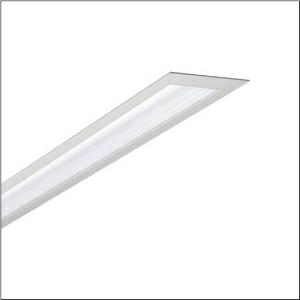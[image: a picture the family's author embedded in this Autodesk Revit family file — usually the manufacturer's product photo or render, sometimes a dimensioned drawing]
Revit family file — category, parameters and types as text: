
# Revit family: silica_r_5mx11dd1w4a_74f3
name_source: partatom
category: Lighting Fixtures
units: mm (PartAtom-declared; Revit-internal decimal feet)

## family parameters
Cut with Voids When Loaded = No
Host = Face
Light Source = No
Part Type = Normal
Room Calculation Point = No
Round Connector Dimension = Use Diameter
Shared = No

## types (1)
- --- (1 x LED, 3140 lm, 22.6 W, 4000K)
    Apparent Load = 23 VA
    CIE Flux Codes = 47 79 96 100 100
    Color Rendering = 80
    Color Temperature = 4000K
    Default Elevation = 1800 mm
    Description = Silica®, office luminaire, of aluminium, opal, light emission: direct distribution, primary light characteristic: symmetric, installation type: recessed, LED rated luminous flux: 3.010 lm, light colour: 840, colour temperature: 4000K, control gear: ECG DALI, with terminal, 3+2-pole, max. 2.5mm², mains connection: 230V, AC, 50/60Hz, rated input power: 24W, luminaire housing, of aluminium, matt pure white (RAL 9010), length: 1.462 mm, width: 93 mm, height: 60mm, end cap, of diecast zinc, pure white (RAL 9010), protection rating (complete): IP20, insulation class (complete): insulation class I (protective earthing), certification: CE, permissible ambient temperature for indoor applications: 0..+35°C, standard: EN 50419, packaging unit: 1 piece
    Height = 0 mm  [stored 0 ft]
    Lamp = 1 x LED
    Lamp Light Flux = 3140 lm
    Lamp Power = 22.6 W
    Lamp count = 1
    Length = 1462 mm
    Luminous efficacy = 139 lm/W
    Manufacturer = Siteco
    ModVariant = No
    Model = 5MX11DD1W4A
    Mounting Place = Ceiling
    Mounting Type = Recessed
    Number of Poles = 1
    OnlyDefault = Yes
    Power Factor = 1
    Product Name = Silica®
    Product group = office luminaire | ceiling recessed
    ProductGroupID = 400
    Protection Class = Protection class I
    Protection Degree = IP 20
    RLX_Detail_Level = 1
    RlxData = <blob elided: 23893 chars, md5=e3de2a6d>
    Socket = socket
    Standby Power = 0 W
    System Light Flux = 3140 lm
    System Power = 23 W
    Type Comments = factory setting: luminous flux: 100 % | dim-lin: 254 | 125 mA
    Type Image = l_1004825.jpg
    URL = http://relux.com
    VarID = @adj_128353
    Voltage = 0 V
    Weight = 0.00 kg
    Width = 93 mm

note: [stored X ft] marks values corroborated as IEEE doubles in the binary element streams (Revit-internal decimal feet)

## geometry (parser evidence)
native form markers: Blend x4, Sweep x14
no freeform markers — native parametric forms only
